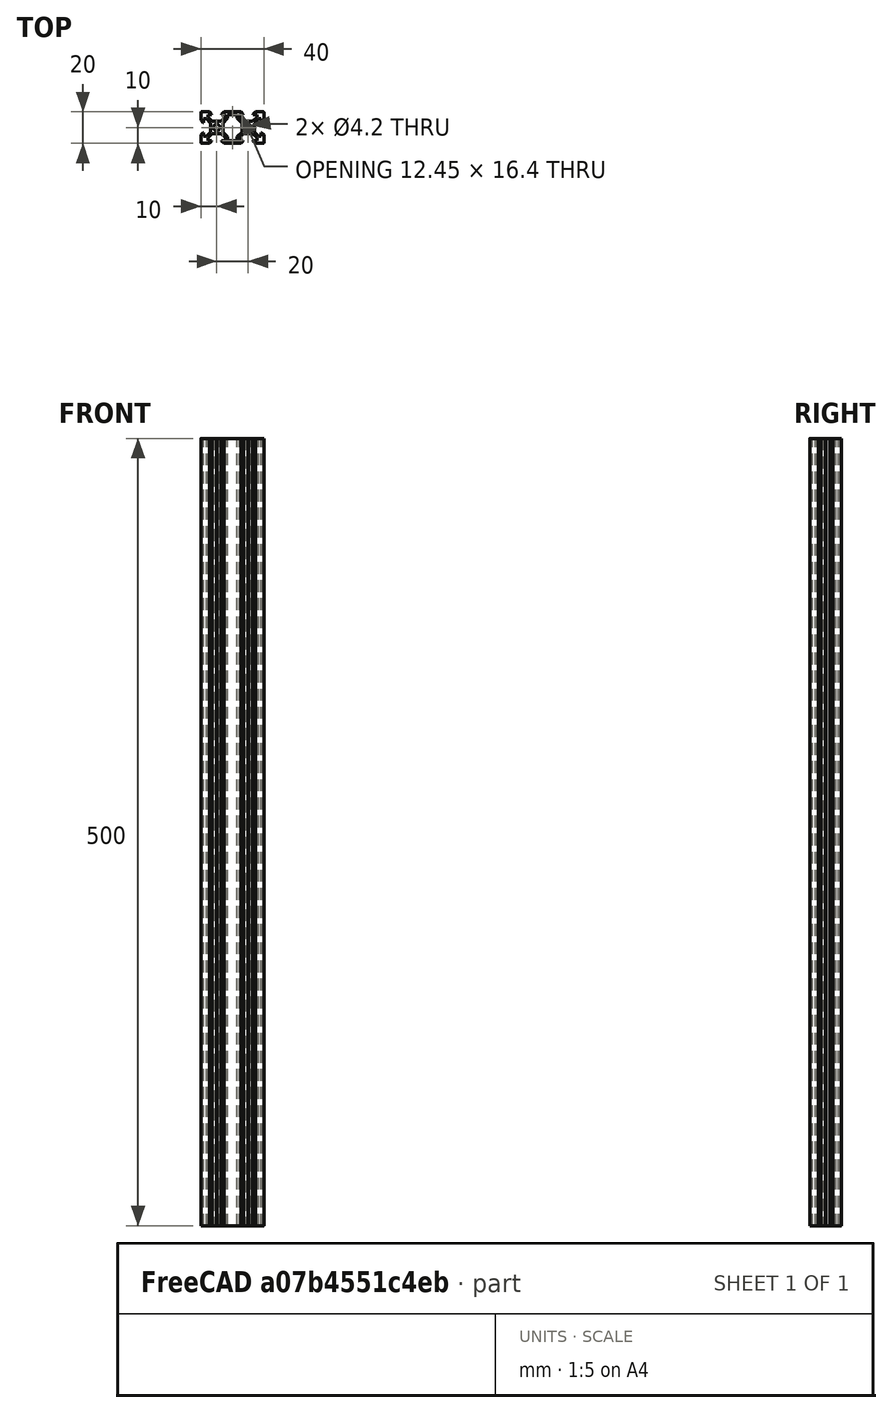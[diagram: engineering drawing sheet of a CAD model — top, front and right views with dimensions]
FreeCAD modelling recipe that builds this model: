
FCSTD DOCUMENT  (FreeCAD 0.20R25645 (Git))
Label: 2040-500
License: All rights reserved
LicenseURL: http://en.wikipedia.org/wiki/All_rights_reserved
objects: Sketcher::SketchObject×1, PartDesign::Pad×1, PartDesign::Body×1
note: 4 computed .brp shape members not serialized (recipe doc carries the construction recipe); baked Part::Feature solids carry a one-line shape summary decoded from their .brp

FEATURE [Sketcher::SketchObject] Sketch
  FullyConstrained = true
  MapMode = 5
  Support = -> [XY_Plane]
  sketch-geometry (114):
    g0: LineSegment StartX=-10 StartY=4.58 StartZ=0 EndX=-10 EndY=9.5 EndZ=0
    g1: LineSegment StartX=-9.5 StartY=10 StartZ=0 EndX=-4.58 EndY=10 EndZ=0
    g2: LineSegment StartX=-5.5 StartY=8.2 StartZ=0 EndX=-3.125 EndY=8.2 EndZ=0
    g3: LineSegment StartX=-8.2 StartY=5.5 StartZ=0 EndX=-8.2 EndY=3.125 EndZ=0
    g4: LineSegment StartX=-0.125 StartY=3.9 StartZ=0 EndX=-2.83934 EndY=3.9 EndZ=0
    g5: LineSegment StartX=-3.9 StartY=2.83934 StartZ=0 EndX=-3.9 EndY=0.125 EndZ=0
    g6: ArcOfCircle CenterX=0 CenterY=3.9 CenterZ=0 NormalX=0 NormalY=0 NormalZ=1 AngleXU=0 Radius=0.125 StartAngle=3.14159 EndAngle=6.28319
    g7: ArcOfCircle CenterX=-3.9 CenterY=0 CenterZ=0 NormalX=0 NormalY=0 NormalZ=1 AngleXU=0 Radius=0.125 StartAngle=4.71239 EndAngle=7.85398
    g8: ArcOfCircle CenterX=-9.5 CenterY=9.5 CenterZ=0 NormalX=0 NormalY=0 NormalZ=1 AngleXU=0 Radius=0.5 StartAngle=1.5708 EndAngle=3.14159
    g9: LineSegment StartX=-5.5 StartY=8.2 StartZ=0 EndX=-5.5 EndY=6.56066 EndZ=0
    g10: LineSegment StartX=-8.2 StartY=5.5 StartZ=0 EndX=-6.56066 EndY=5.5 EndZ=0
    g11: LineSegment StartX=-4.58 StartY=10 StartZ=0 EndX=-3.125 EndY=8.545 EndZ=0
    g12: LineSegment StartX=-3.125 StartY=8.545 StartZ=0 EndX=-3.125 EndY=8.2 EndZ=0
    g13: LineSegment StartX=-10 StartY=4.58 StartZ=0 EndX=-8.545 EndY=3.125 EndZ=0
    g14: LineSegment StartX=-8.545 StartY=3.125 StartZ=0 EndX=-8.2 EndY=3.125 EndZ=0
    g15: LineSegment StartX=-5.5 StartY=6.56066 StartZ=0 EndX=-2.83934 EndY=3.9 EndZ=0
    g16: LineSegment StartX=-6.56066 StartY=5.5 StartZ=0 EndX=-3.9 EndY=2.83934 EndZ=0
    g17: Circle CenterX=0 CenterY=0 CenterZ=0 NormalX=0 NormalY=0 NormalZ=1 AngleXU=0 Radius=2.1
    g18: LineSegment StartX=0.125 StartY=3.9 StartZ=0 EndX=2.83934 EndY=3.9 EndZ=0
    g19: LineSegment StartX=2.83934 StartY=3.9 StartZ=0 EndX=5.5 EndY=6.56066 EndZ=0
    g20: LineSegment StartX=5.5 StartY=6.56066 StartZ=0 EndX=5.5 EndY=8.2 EndZ=0
    g21: LineSegment StartX=3.125 StartY=8.2 StartZ=0 EndX=3.125 EndY=8.545 EndZ=0
    g22: LineSegment StartX=5.5 StartY=8.2 StartZ=0 EndX=3.125 EndY=8.2 EndZ=0
    g23: LineSegment StartX=7 StartY=5.93934 StartZ=0 EndX=3.9 EndY=2.83934 EndZ=0
    g24: LineSegment StartX=3.9 StartY=2.83934 StartZ=0 EndX=3.9 EndY=0.125 EndZ=0
    g25: ArcOfCircle CenterX=3.9 CenterY=0 CenterZ=0 NormalX=0 NormalY=0 NormalZ=1 AngleXU=0 Radius=0.125 StartAngle=1.5708 EndAngle=4.71239
    g26: LineSegment StartX=3.9 StartY=-0.125 StartZ=0 EndX=3.9 EndY=-2.83934 EndZ=0
    g27: LineSegment StartX=3.9 StartY=-2.83934 StartZ=0 EndX=7 EndY=-5.93934 EndZ=0
    g28: LineSegment StartX=4.58 StartY=-10 StartZ=0 EndX=3.125 EndY=-8.545 EndZ=0
    g29: LineSegment StartX=2.83934 StartY=-3.9 StartZ=0 EndX=5.5 EndY=-6.56066 EndZ=0
    g30: LineSegment StartX=3.125 StartY=-8.545 StartZ=0 EndX=3.125 EndY=-8.2 EndZ=0
    g31: LineSegment StartX=3.125 StartY=-8.2 StartZ=0 EndX=5.5 EndY=-8.2 EndZ=0
    g32: LineSegment StartX=5.5 StartY=-8.2 StartZ=0 EndX=5.5 EndY=-6.56066 EndZ=0
    g33: ArcOfCircle CenterX=0 CenterY=-3.9 CenterZ=0 NormalX=0 NormalY=0 NormalZ=1 AngleXU=0 Radius=0.125 StartAngle=0 EndAngle=3.14159
    g34: LineSegment StartX=0.125 StartY=-3.9 StartZ=0 EndX=2.83934 EndY=-3.9 EndZ=0
    g35: LineSegment StartX=-0.125 StartY=-3.9 StartZ=0 EndX=-2.83934 EndY=-3.9 EndZ=0
    g36: LineSegment StartX=-3.9 StartY=-0.125 StartZ=0 EndX=-3.9 EndY=-2.83934 EndZ=0
    g37: LineSegment StartX=-3.9 StartY=-2.83934 StartZ=0 EndX=-6.56066 EndY=-5.5 EndZ=0
    g38: LineSegment StartX=-6.56066 StartY=-5.5 StartZ=0 EndX=-8.2 EndY=-5.5 EndZ=0
    g39: LineSegment StartX=-8.2 StartY=-5.5 StartZ=0 EndX=-8.2 EndY=-3.125 EndZ=0
    g40: LineSegment StartX=-8.2 StartY=-3.125 StartZ=0 EndX=-8.545 EndY=-3.125 EndZ=0
    g41: LineSegment StartX=-8.545 StartY=-3.125 StartZ=0 EndX=-10 EndY=-4.58 EndZ=0
    g42: LineSegment StartX=-10 StartY=-4.58 StartZ=0 EndX=-10 EndY=-9.5 EndZ=0
    g43: ArcOfCircle CenterX=-9.5 CenterY=-9.5 CenterZ=0 NormalX=0 NormalY=0 NormalZ=1 AngleXU=0 Radius=0.5 StartAngle=3.14159 EndAngle=4.71239
    g44: LineSegment StartX=-9.5 StartY=-10 StartZ=0 EndX=-4.58 EndY=-10 EndZ=0
    g45: LineSegment StartX=-4.58 StartY=-10 StartZ=0 EndX=-3.125 EndY=-8.545 EndZ=0
    g46: LineSegment StartX=-2.83934 StartY=-3.9 StartZ=0 EndX=-5.5 EndY=-6.56066 EndZ=0
    g47: LineSegment StartX=-5.5 StartY=-6.56066 StartZ=0 EndX=-5.5 EndY=-8.2 EndZ=0
    g48: LineSegment StartX=-5.5 StartY=-8.2 StartZ=0 EndX=-3.125 EndY=-8.2 EndZ=0
    g49: LineSegment StartX=-3.125 StartY=-8.545 StartZ=0 EndX=-3.125 EndY=-8.2 EndZ=0
    g50: LineSegment StartX=3.125 StartY=8.545 StartZ=0 EndX=4.58 EndY=10 EndZ=0
    g51: LineSegment StartX=-3.9 StartY=2.83934 StartZ=0 EndX=-2.83934 EndY=3.9 EndZ=0
    g52: LineSegment StartX=3.9 StartY=2.83934 StartZ=0 EndX=2.83934 EndY=3.9 EndZ=0
    g53: LineSegment StartX=4.58 StartY=10 StartZ=0 EndX=15.42 EndY=10 EndZ=0
    g54: LineSegment StartX=4.58 StartY=-10 StartZ=0 EndX=15.42 EndY=-10 EndZ=0
    g55: LineSegment StartX=7 StartY=5.93934 StartZ=0 EndX=7 EndY=8.2 EndZ=0
    g56: LineSegment StartX=5.5 StartY=8.2 StartZ=0 EndX=7 EndY=8.2 EndZ=0
    g57: LineSegment StartX=7 StartY=-5.93934 StartZ=0 EndX=7 EndY=-8.2 EndZ=0
    g58: LineSegment StartX=7 StartY=8.2 StartZ=0 EndX=13 EndY=8.2 EndZ=0
    g59: LineSegment StartX=15.42 StartY=10 StartZ=0 EndX=16.875 EndY=8.545 EndZ=0
    g60: LineSegment StartX=16.875 StartY=8.545 StartZ=0 EndX=16.875 EndY=8.2 EndZ=0
    g61: LineSegment StartX=16.875 StartY=8.2 StartZ=0 EndX=14.5 EndY=8.2 EndZ=0
    g62: LineSegment StartX=15.42 StartY=-10 StartZ=0 EndX=16.875 EndY=-8.545 EndZ=0
    g63: LineSegment StartX=16.875 StartY=-8.545 StartZ=0 EndX=16.875 EndY=-8.2 EndZ=0
    g64: LineSegment StartX=16.875 StartY=-8.2 StartZ=0 EndX=14.5 EndY=-8.2 EndZ=0
    g65: LineSegment StartX=7 StartY=-8.2 StartZ=0 EndX=13 EndY=-8.2 EndZ=0
    g66: LineSegment StartX=13 StartY=8.2 StartZ=0 EndX=14.5 EndY=8.2 EndZ=0
    g67: LineSegment StartX=13 StartY=8.2 StartZ=0 EndX=13 EndY=5.93934 EndZ=0
    g68: LineSegment StartX=13 StartY=-8.2 StartZ=0 EndX=13 EndY=-5.93934 EndZ=0
    g69: LineSegment StartX=14.5 StartY=8.2 StartZ=0 EndX=14.5 EndY=6.56066 EndZ=0
    g70: LineSegment StartX=14.5 StartY=-8.2 StartZ=0 EndX=14.5 EndY=-6.56066 EndZ=0
    g71: LineSegment StartX=13 StartY=5.93934 StartZ=0 EndX=16.1 EndY=2.83934 EndZ=0
    g72: LineSegment StartX=14.5 StartY=6.56066 StartZ=0 EndX=17.1607 EndY=3.9 EndZ=0
    g73: LineSegment StartX=13 StartY=-5.93934 StartZ=0 EndX=16.1 EndY=-2.83934 EndZ=0
    g74: LineSegment StartX=14.5 StartY=-6.56066 StartZ=0 EndX=17.1607 EndY=-3.9 EndZ=0
    g75: LineSegment StartX=16.1 StartY=2.83934 StartZ=0 EndX=16.1 EndY=0.125 EndZ=0
    g76: LineSegment StartX=16.1 StartY=-2.83934 StartZ=0 EndX=16.1 EndY=-0.125 EndZ=0
    g77: ArcOfCircle CenterX=16.1 CenterY=0 CenterZ=0 NormalX=0 NormalY=0 NormalZ=1 AngleXU=0 Radius=0.125 StartAngle=4.71239 EndAngle=7.85398
    g78: LineSegment StartX=17.1607 StartY=3.9 StartZ=0 EndX=19.875 EndY=3.9 EndZ=0
    g79: LineSegment StartX=17.1607 StartY=-3.9 StartZ=0 EndX=19.875 EndY=-3.9 EndZ=0
    g80: LineSegment StartX=20.125 StartY=3.9 StartZ=0 EndX=22.8393 EndY=3.9 EndZ=0
    g81: LineSegment StartX=20.125 StartY=-3.9 StartZ=0 EndX=22.8393 EndY=-3.9 EndZ=0
    g82: ArcOfCircle CenterX=20 CenterY=-3.9 CenterZ=0 NormalX=0 NormalY=0 NormalZ=1 AngleXU=0 Radius=0.125 StartAngle=-9e-16 EndAngle=3.14159
    g83: ArcOfCircle CenterX=20 CenterY=3.9 CenterZ=0 NormalX=0 NormalY=0 NormalZ=1 AngleXU=0 Radius=0.125 StartAngle=3.14159 EndAngle=6.28319
    g84: Circle CenterX=20 CenterY=0 CenterZ=0 NormalX=0 NormalY=0 NormalZ=1 AngleXU=0 Radius=2.1
    g85: LineSegment StartX=22.8393 StartY=3.9 StartZ=0 EndX=25.5 EndY=6.56066 EndZ=0
    g86: LineSegment StartX=22.8393 StartY=-3.9 StartZ=0 EndX=25.5 EndY=-6.56066 EndZ=0
    g87: LineSegment StartX=25.5 StartY=6.56066 StartZ=0 EndX=25.5 EndY=8.2 EndZ=0
    g88: LineSegment StartX=25.5 StartY=-6.56066 StartZ=0 EndX=25.5 EndY=-8.2 EndZ=0
    g89: LineSegment StartX=25.5 StartY=8.2 StartZ=0 EndX=23.125 EndY=8.2 EndZ=0
    g90: LineSegment StartX=25.5 StartY=-8.2 StartZ=0 EndX=23.125 EndY=-8.2 EndZ=0
    g91: LineSegment StartX=23.125 StartY=8.2 StartZ=0 EndX=23.125 EndY=8.545 EndZ=0
    g92: LineSegment StartX=23.125 StartY=-8.2 StartZ=0 EndX=23.125 EndY=-8.545 EndZ=0
    g93: LineSegment StartX=23.125 StartY=8.545 StartZ=0 EndX=24.58 EndY=10 EndZ=0
    g94: LineSegment StartX=23.125 StartY=-8.545 StartZ=0 EndX=24.58 EndY=-10 EndZ=0
    g95: LineSegment StartX=24.58 StartY=10 StartZ=0 EndX=29.5 EndY=10 EndZ=0
    g96: LineSegment StartX=24.58 StartY=-10 StartZ=0 EndX=29.5 EndY=-10 EndZ=0
    g97: ArcOfCircle CenterX=29.5 CenterY=9.5 CenterZ=0 NormalX=0 NormalY=0 NormalZ=1 AngleXU=0 Radius=0.5 StartAngle=9e-16 EndAngle=1.5708
    g98: ArcOfCircle CenterX=29.5 CenterY=-9.5 CenterZ=0 NormalX=0 NormalY=0 NormalZ=1 AngleXU=0 Radius=0.5 StartAngle=4.71239 EndAngle=6.28319
    g99: LineSegment StartX=30 StartY=9.5 StartZ=0 EndX=30 EndY=4.58 EndZ=0
    g100: LineSegment StartX=30 StartY=-9.5 StartZ=0 EndX=30 EndY=-4.58 EndZ=0
    g101: LineSegment StartX=30 StartY=-4.58 StartZ=0 EndX=28.545 EndY=-3.125 EndZ=0
    g102: LineSegment StartX=30 StartY=4.58 StartZ=0 EndX=28.545 EndY=3.125 EndZ=0
    g103: LineSegment StartX=28.545 StartY=3.125 StartZ=0 EndX=28.2 EndY=3.125 EndZ=0
    g104: LineSegment StartX=28.545 StartY=-3.125 StartZ=0 EndX=28.2 EndY=-3.125 EndZ=0
    g105: LineSegment StartX=28.2 StartY=3.125 StartZ=0 EndX=28.2 EndY=5.5 EndZ=0
    g106: LineSegment StartX=28.2 StartY=-3.125 StartZ=0 EndX=28.2 EndY=-5.5 EndZ=0
    g107: LineSegment StartX=28.2 StartY=5.5 StartZ=0 EndX=26.5607 EndY=5.5 EndZ=0
    g108: LineSegment StartX=28.2 StartY=-5.5 StartZ=0 EndX=26.5607 EndY=-5.5 EndZ=0
    g109: LineSegment StartX=26.5607 StartY=5.5 StartZ=0 EndX=23.9 EndY=2.83934 EndZ=0
    g110: LineSegment StartX=26.5607 StartY=-5.5 StartZ=0 EndX=23.9 EndY=-2.83934 EndZ=0
    g111: LineSegment StartX=23.9 StartY=2.83934 StartZ=0 EndX=23.9 EndY=0.125 EndZ=0
    g112: LineSegment StartX=23.9 StartY=-2.83934 StartZ=0 EndX=23.9 EndY=-0.125 EndZ=0
    g113: ArcOfCircle CenterX=23.9 CenterY=3.14e-14 CenterZ=0 NormalX=0 NormalY=0 NormalZ=1 AngleXU=0 Radius=0.125 StartAngle=1.5708 EndAngle=4.71236
  constraints (345):
    c: Diameter(g17) = 4.2
    c: Radius(g25) = 0.125
    c: Coincident(g-1,g17)
    c: DistanceY(g43,g1) = 20
    c: Radius(g43) = 0.5
    c: DistanceX(g42,g17) = 10
    c: DistanceY(g43,g17) = 10
    c: Distance(g5,g4) = 1.5
    c: DistanceY(g18,g20) = 4.3
    c: DistanceX(g11,g21) = 6.25
    c: DistanceX(g1,g50) = 9.16
    c: DistanceX(g2,g20) = 11
    c: Coincident(g6,g18)
    c: Coincident(g6,g4)
    c: Coincident(g4,g15)
    c: Coincident(g18,g19)
    c: Coincident(g5,g16)
    c: Coincident(g16,g10)
    c: Coincident(g15,g9)
    c: Coincident(g12,g2)
    c: Coincident(g2,g9)
    c: Coincident(g12,g11)
    c: Coincident(g1,g11)
    c: Coincident(g22,g21)
    c: Coincident(g50,g21)
    c: Coincident(g22,g20)
    c: Coincident(g19,g20)
    c: Coincident(g0,g13)
    c: Coincident(g14,g13)
    c: Coincident(g14,g3)
    c: Coincident(g3,g10)
    c: Coincident(g5,g7)
    c: Coincident(g36,g7)
    c: Coincident(g37,g36)
    c: Coincident(g38,g37)
    c: Coincident(g38,g39)
    c: Coincident(g40,g39)
    c: Coincident(g41,g40)
    c: Coincident(g42,g41)
    c: Coincident(g44,g45)
    c: Coincident(g49,g45)
    c: Coincident(g48,g49)
    c: Coincident(g48,g47)
    c: Coincident(g46,g47)
    c: Coincident(g35,g46)
    c: Coincident(g33,g35)
    c: Coincident(g34,g33)
    c: Coincident(g34,g29)
    c: Coincident(g32,g29)
    c: Coincident(g31,g32)
    c: Coincident(g31,g30)
    c: Coincident(g28,g30)
    c: Coincident(g27,g26)
    c: Coincident(g24,g23)
    c: Coincident(g26,g25)
    c: Coincident(g25,g24)
    c: Vertical(g0)
    c: Horizontal(g1)
    c: Equal(g0,g1)
    c: Horizontal(g4)
    c: PointOnObject(g6,g-2)
    c: Horizontal(g18)
    c: Horizontal(g4,g6)
    c: Horizontal(g6,g6)
    c: Parallel(g13,g11)
    c: Horizontal(g14)
    c: Vertical(g12)
    c: Equal(g14,g12)
    c: Vertical(g3)
    c: Horizontal(g2)
    c: Equal(g3,g2)
    c: Equal(g10,g9)
    c: Horizontal(g10)
    c: Vertical(g9)
    c: Parallel(g16,g15)
    c: Equal(g13,g11)
    c: Tangent(g8,g0) = 1.5708
    c: PointOnObject(g7,g-1)
    c: Vertical(g5)
    c: Vertical(g36)
    c: Vertical(g7,g7)
    c: Vertical(g7,g5)
    c: Horizontal(g38)
    c: Vertical(g39)
    c: Horizontal(g40)
    c: Vertical(g42)
    c: Equal(g36,g5)
    c: Equal(g37,g16)
    c: Perpendicular(g16,g37)
    c: Equal(g38,g10)
    c: Equal(g39,g3)
    c: Equal(g40,g14)
    c: Equal(g41,g13)
    c: Perpendicular(g41,g13)
    c: Equal(g42,g0)
    c: Tangent(g43,g42) = -1.5708
    c: Tangent(g43,g44) = -1.5708
    c: Tangent(g8,g1) = 1.5708
    c: Equal(g43,g8)
    c: Horizontal(g44)
    c: Equal(g44,g42)
    c: Equal(g41,g45)
    c: Parallel(g41,g45)
    c: Vertical(g49)
    c: Equal(g49,g40)
    c: Horizontal(g48)
    c: Vertical(g47)
    c: Equal(g47,g38)
    c: Equal(g46,g37)
    c: Parallel(g46,g37)
    c: PointOnObject(g33,g-2)
    c: Horizontal(g33,g33)
    c: Horizontal(g33,g33)
    c: Horizontal(g35)
    c: Equal(g35,g36)
    c: Horizontal(g34)
    c: Vertical(g32)
    c: Perpendicular(g46,g29)
    c: Equal(g29,g46)
    c: Equal(g32,g47)
    c: Horizontal(g31)
    c: Equal(g31,g48)
    c: Vertical(g30)
    c: Equal(g30,g49)
    c: Perpendicular(g28,g45)
    c: Equal(g28,g45)
    c: Parallel(g29,g27)
    c: PointOnObject(g25,g-1)
    c: Vertical(g26)
    c: Vertical(g25,g24)
    c: Vertical(g24,g25)
    c: Equal(g34,g26)
    c: Equal(g33,g7)
    c: Equal(g7,g6)
    c: Vertical(g24)
    c: Equal(g26,g24)
    c: Equal(g4,g5)
    c: Equal(g4,g18)
    c: Parallel(g23,g19)
    c: Vertical(g20)
    c: Horizontal(g22)
    c: Equal(g22,g2)
    c: Vertical(g21)
    c: Equal(g11,g50)
    c: Horizontal(g2,g21)
    c: Vertical(g10,g37)
    c: Angle(g50,g11) = 1.5708
    c: DistanceY(g2,g1) = 1.8
    c: Equal(g21,g12)
    c: Horizontal(g36,g26)
    c: Vertical(g29,g18)
    c: Coincident(g51,g5)
    c: Coincident(g51,g4)
    c: Coincident(g52,g23)
    c: Coincident(g52,g18)
    c: Equal(g52,g51)
    c: Equal(g15,g19)
    c: Equal(g20,g9)
    c: Horizontal(g53)
    c: Horizontal(g54)
    c: Coincident(g55,g23)
    c: Vertical(g55)
    c: Horizontal(g55,g20)
    c: Coincident(g56,g20)
    c: Coincident(g56,g55)
    c: Equal(g56,g52)
    c: Coincident(g57,g27)
    c: Horizontal(g31,g57)
    c: Vertical(g57)
    c: Vertical(g27,g23)
    c: Coincident(g58,g55)
    c: Horizontal(g58)
    c: Coincident(g59,g53)
    c: Coincident(g60,g59)
    c: Vertical(g60)
    c: Coincident(g61,g60)
    c: Horizontal(g61)
    c: Coincident(g62,g54)
    c: Coincident(g63,g62)
    c: Vertical(g63)
    c: Coincident(g64,g63)
    c: Horizontal(g64)
    c: Coincident(g65,g57)
    c: Horizontal(g65)
    c: Equal(g22,g61)
    c: Equal(g64,g31)
    c: Equal(g59,g50)
    c: Equal(g62,g28)
    c: Equal(g21,g60)
    c: Equal(g30,g63)
    c: Perpendicular(g59,g50)
    c: Perpendicular(g62,g28)
    c: Equal(g58,g65)
    c: Coincident(g66,g58)
    c: Coincident(g66,g61)
    c: Equal(g56,g66)
    c: Coincident(g67,g58)
    c: Vertical(g67)
    c: Coincident(g68,g65)
    c: Vertical(g68)
    c: Coincident(g69,g61)
    c: Vertical(g69)
    c: Coincident(g70,g64)
    c: Vertical(g70)
    c: Equal(g55,g67)
    c: Equal(g57,g68)
    c: Equal(g20,g69)
    c: Equal(g32,g70)
    c: Coincident(g71,g67)
    c: Coincident(g72,g69)
    c: Coincident(g73,g68)
    c: Coincident(g74,g70)
    c: Equal(g23,g71)
    c: Perpendicular(g71,g23)
    c: Equal(g27,g73)
    c: Perpendicular(g73,g27)
    c: Equal(g72,g19)
    c: Perpendicular(g19,g72)
    c: Equal(g74,g29)
    c: Perpendicular(g29,g74)
    c: Coincident(g75,g71)
    c: Vertical(g75)
    c: Coincident(g76,g73)
    c: Vertical(g76)
    c: Equal(g24,g75)
    c: PointOnObject(g77,g-1)
    c: Coincident(g77,g75)
    c: Coincident(g77,g76)
    c: Equal(g25,g77)
    c: Coincident(g78,g72)
    c: Horizontal(g78)
    c: Coincident(g79,g74)
    c: Horizontal(g79)
    c: Equal(g18,g78)
    c: Equal(g34,g79)
    c: Horizontal(g80)
    c: Horizontal(g81)
    c: Equal(g79,g81)
    c: Equal(g78,g80)
    c: Horizontal(g78,g80)
    c: Horizontal(g79,g81)
    c: Coincident(g82,g79)
    c: Coincident(g82,g81)
    c: Coincident(g83,g78)
    c: Coincident(g83,g80)
    c: Equal(g77,g83)
    c: Equal(g77,g82)
    c: Horizontal(g83,g78)
    c: Horizontal(g79,g82)
    c: PointOnObject(g84,g-1)
    c: Equal(g17,g84)
    c: DistanceX(g17,g84) = 20
    c: Vertical(g70,g69)
    c: Coincident(g53,g50)
    c: Coincident(g54,g28)
    c: Vertical(g83,g84)
    c: Coincident(g85,g80)
    c: Coincident(g86,g81)
    c: Equal(g85,g19)
    c: Equal(g86,g29)
    c: Parallel(g19,g85)
    c: Parallel(g86,g29)
    c: Coincident(g87,g85)
    c: Coincident(g88,g86)
    c: Vertical(g88)
    c: Vertical(g87)
    c: Equal(g20,g87)
    c: Equal(g32,g88)
    c: Coincident(g89,g87)
    c: Horizontal(g89)
    c: Coincident(g90,g88)
    c: Horizontal(g90)
    c: Equal(g22,g89)
    c: Equal(g31,g90)
    c: Coincident(g91,g89)
    c: Vertical(g91)
    c: Coincident(g92,g90)
    c: Vertical(g92)
    c: Equal(g21,g91)
    c: Equal(g92,g30)
    c: Coincident(g93,g91)
    c: Coincident(g94,g92)
    c: Coincident(g95,g93)
    c: Horizontal(g95)
    c: Coincident(g96,g94)
    c: Horizontal(g96)
    c: Equal(g50,g93)
    c: Perpendicular(g93,g59)
    c: Equal(g94,g28)
    c: Perpendicular(g94,g62)
    c: Equal(g1,g95)
    c: Equal(g44,g96)
    c: Coincident(g97,g95)
    c: Coincident(g98,g96)
    c: Equal(g8,g97)
    c: Horizontal(g8,g97)
    c: Horizontal(g97,g97)
    c: Horizontal(g98,g43)
    c: Equal(g98,g43)
    c: Horizontal(g98,g98)
    c: Coincident(g99,g97)
    c: Vertical(g99)
    c: Coincident(g100,g98)
    c: Vertical(g100)
    c: Equal(g0,g99)
    c: Equal(g42,g100)
    c: Coincident(g101,g100)
    c: Coincident(g102,g99)
    c: Equal(g101,g41)
    c: Perpendicular(g101,g41)
    c: Equal(g102,g13)
    c: Perpendicular(g13,g102)
    c: Coincident(g103,g102)
    c: Horizontal(g103)
    c: Coincident(g104,g101)
    c: Horizontal(g104)
    c: Equal(g103,g14)
    c: Equal(g104,g40)
    c: Coincident(g105,g103)
    c: Vertical(g105)
    c: Coincident(g106,g104)
    c: Vertical(g106)
    c: Equal(g3,g105)
    c: Equal(g106,g39)
    c: Coincident(g107,g105)
    c: Horizontal(g107)
    c: Coincident(g108,g106)
    c: Horizontal(g108)
    c: Equal(g38,g108)
    c: Equal(g10,g107)
    c: Coincident(g109,g107)
    c: Coincident(g110,g108)
    c: Equal(g110,g37)
    c: Perpendicular(g37,g110)
    c: Equal(g109,g16)
    c: Perpendicular(g16,g109)
    c: Coincident(g111,g109)
    c: Vertical(g111)
    c: Coincident(g112,g110)
    c: Vertical(g112)
    c: Equal(g76,g112)
    c: Equal(g75,g111)
    c: Coincident(g113,g111)
    c: Coincident(g113,g112)
    c: Vertical(g113,g111)
FEATURE [PartDesign::Pad] Pad
  Direction = (0,0,1)
  Length = 500
  Length2 = 100
  Profile = -> Sketch
  Type = 0
FEATURE [PartDesign::Body] Body  label="2020-500"
  Group = -> [Sketch,Pad]
  Origin = -> Origin
  Tip = -> Pad
